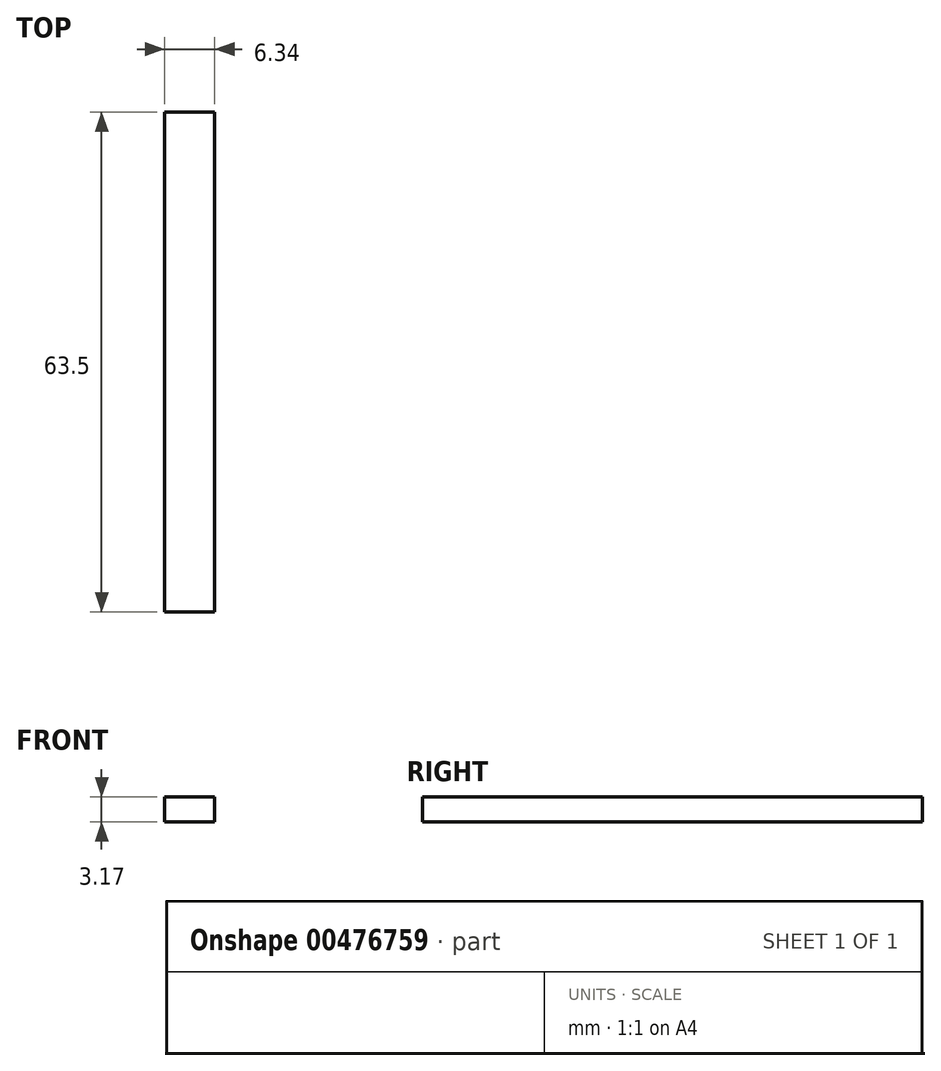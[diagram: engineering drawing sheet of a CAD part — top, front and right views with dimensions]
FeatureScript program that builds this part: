
annotation { "Feature Type Name" : "Feature", "Feature Type Description" : "" }
export const myFeature = defineFeature(function(context is Context, id is Id, definition is map)
    precondition{}
    {
        {
            var Q0;
            Q0=qCreatedBy(makeId("Top.planeOp"),FACE);
            var sketch = newSketch(context, id + "F0", { "sketchPlane" : qUnion([Q0])});
            skLineSegment(sketch, "E0.bottom", {"start": v(3.18, 31.75) * mm, "end": v(-3.17, 31.75) * mm});
            skLineSegment(sketch, "E0.top", {"start": v(3.18, -31.75) * mm, "end": v(-3.18, -31.75) * mm});
            skLineSegment(sketch, "E0.left", {"start": v(3.18, 31.75) * mm, "end": v(3.18, -31.75) * mm});
            skLineSegment(sketch, "E0.right", {"start": v(-3.17, 31.75) * mm, "end": v(-3.18, -31.75) * mm});
            skPoint(sketch, "E0.middle", {"position": v(0, 0) * mm});
            skSolve(sketch);
        }
        {
            var Q0;
            Q0=makeQuery(id+"F0.imprint","IMPRINT",FACE,{"disambiguationData":[TD([[makeQuery(id+"F0.imprint","IMPRINT",EDGE,{"derivedFrom":sQuery(id+"F0.wireOp",EDGE,"E0.bottom")}),1.0]])]});
            extrude(context, id + "F1", {"entities" : qUnion([Q0]), "oppositeDirection" : true, "depth" : 3.17 * mm});
        }
    });
